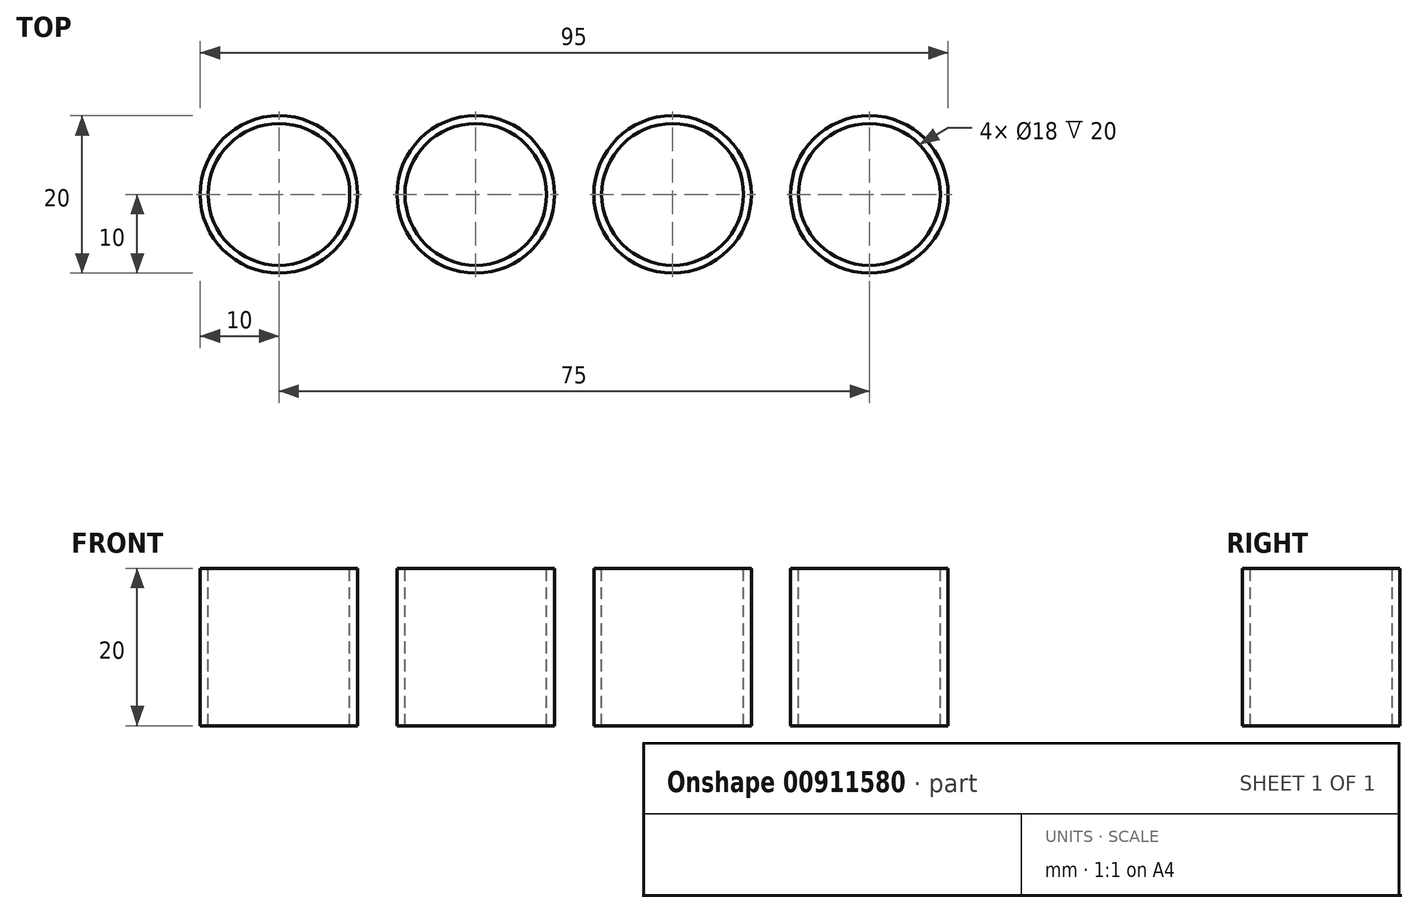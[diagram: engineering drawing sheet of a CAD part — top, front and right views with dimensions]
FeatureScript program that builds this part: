
annotation { "Feature Type Name" : "Feature", "Feature Type Description" : "" }
export const myFeature = defineFeature(function(context is Context, id is Id, definition is map)
    precondition{}
    {
        {
            var Q0;
            Q0=qCreatedBy(makeId("Top.planeOp"),FACE);
            var sketch = newSketch(context, id + "F0", { "sketchPlane" : qUnion([Q0])});
            skCircle(sketch, "E0", {"center": v(0, 0) * mm, "radius": 10 * mm});
            skCircle(sketch, "E1.1.0.0", {"center": v(25, 0) * mm, "radius": 10 * mm});
            skCircle(sketch, "E1.2.0.0", {"center": v(50, 0) * mm, "radius": 10 * mm});
            skLineSegment(sketch, "E1.direction1", {"start": v(0, 0) * mm, "end": v(25, 0) * mm, "construction": true});
            skCircle(sketch, "E2.0.3.0", {"center": v(75, 0) * mm, "radius": 10 * mm});
            skCircle(sketch, "E3", {"center": v(0, 0) * mm, "radius": 9 * mm});
            skCircle(sketch, "E4.1.0.0", {"center": v(25, 0) * mm, "radius": 9 * mm});
            skCircle(sketch, "E4.2.0.0", {"center": v(50, 0) * mm, "radius": 9 * mm});
            skCircle(sketch, "E4.3.0.0", {"center": v(75, 0) * mm, "radius": 9 * mm});
            skLineSegment(sketch, "E5.bottom", {"start": v(-22.5, 20) * mm, "end": v(97.5, 20) * mm});
            skLineSegment(sketch, "E5.top", {"start": v(-22.5, -15) * mm, "end": v(97.5, -15) * mm});
            skLineSegment(sketch, "E5.left", {"start": v(-22.5, 20) * mm, "end": v(-22.5, -15) * mm});
            skLineSegment(sketch, "E5.right", {"start": v(97.5, 20) * mm, "end": v(97.5, -15) * mm});
            skSolve(sketch);
        }
        {
            var Q0;
            Q0=makeQuery(id+"F0.imprint","IMPRINT",FACE,{"disambiguationData":[TD([[makeQuery(id+"F0.imprint","IMPRINT",EDGE,{"derivedFrom":sQuery(id+"F0.wireOp",EDGE,"E0")}),1.0]])]});
            var Q1;
            Q1=makeQuery(id+"F0.imprint","IMPRINT",FACE,{"disambiguationData":[TD([[makeQuery(id+"F0.imprint","IMPRINT",EDGE,{"derivedFrom":sQuery(id+"F0.wireOp",EDGE,"E1.1.0.0")}),1.0]])]});
            var Q2;
            Q2=makeQuery(id+"F0.imprint","IMPRINT",FACE,{"disambiguationData":[TD([[makeQuery(id+"F0.imprint","IMPRINT",EDGE,{"derivedFrom":sQuery(id+"F0.wireOp",EDGE,"E1.2.0.0")}),1.0]])]});
            var Q3;
            Q3=makeQuery(id+"F0.imprint","IMPRINT",FACE,{"disambiguationData":[TD([[makeQuery(id+"F0.imprint","IMPRINT",EDGE,{"derivedFrom":sQuery(id+"F0.wireOp",EDGE,"E2.0.3.0")}),1.0]])]});
            extrude(context, id + "F1", {"entities" : qUnion([Q0, Q1, Q2, Q3]), "oppositeDirection" : true, "depth" : 20 * mm, "offsetDistance" : 25 * mm});
        }
    });
